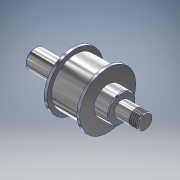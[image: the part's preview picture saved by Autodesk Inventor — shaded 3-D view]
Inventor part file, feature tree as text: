
AUTODESK INVENTOR PART (.ipt)
format: ipt  version: 2018 (Build 220112000, 112)  size: 153,600 bytes
history: native  units: mm
features: sketch x5, extrude x3, revolve x1, thread x1, chamfer x1
ambient origin geometry x8: Origin, YZ Plane, XZ Plane, XY Plane, X Axis, Y Axis, Z Axis, Center Point
bodies: Solido1 (feature_tree)
feature tree (11):
  revolve  "Rivoluzione1"
  sketch  "Schizzo3"
  extrude  "Estrusione2"  Depth=7.0mm
  extrude  "Estrusione3"  Depth=3.0mm
  thread  "Filettatura1"
  extrude  "Estrusione4"  Depth=3.0mm
  chamfer  "Smusso1"  Distance=7.0mm
  sketch  "Schizzo1"
  sketch  "Schizzo4"
  sketch  "Schizzo5"
  sketch  "Schizzo6"
